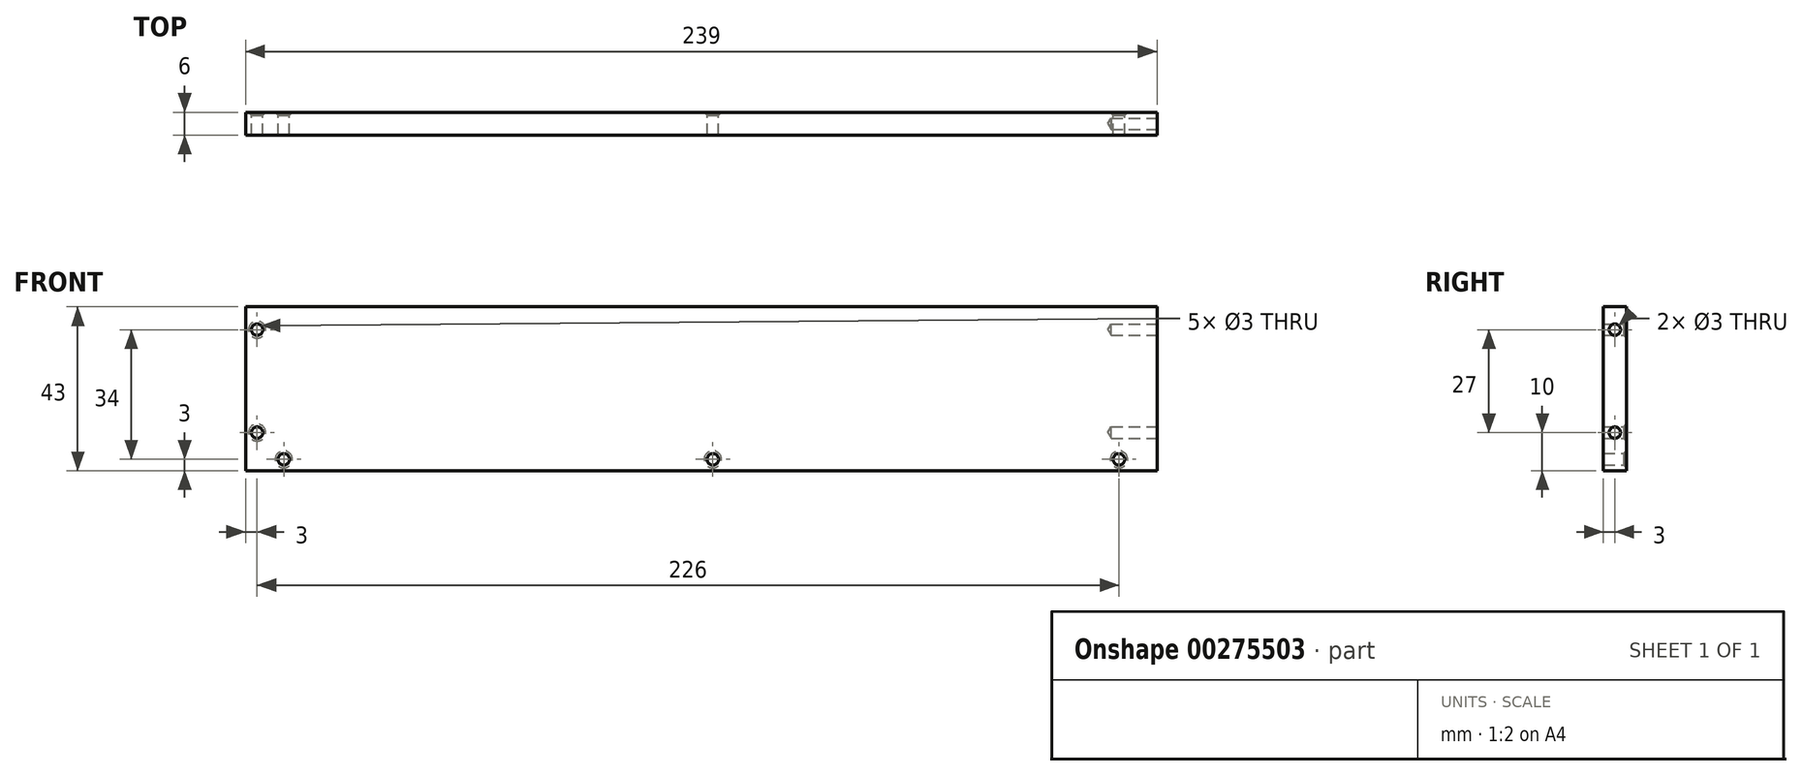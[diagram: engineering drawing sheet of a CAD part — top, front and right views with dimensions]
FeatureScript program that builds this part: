
annotation { "Feature Type Name" : "Feature", "Feature Type Description" : "" }
export const myFeature = defineFeature(function(context is Context, id is Id, definition is map)
    precondition{}
    {
        {
            var Q0;
            Q0=qCreatedBy(makeId("Top.planeOp"),FACE);
            var sketch = newSketch(context, id + "F0", { "sketchPlane" : qUnion([Q0])});
            skLineSegment(sketch, "E0.bottom", {"start": v(0, 0) * mm, "end": v(239, 0) * mm});
            skLineSegment(sketch, "E0.top", {"start": v(0, 6) * mm, "end": v(239, 6) * mm});
            skLineSegment(sketch, "E0.left", {"start": v(0, 0) * mm, "end": v(0, 6) * mm});
            skLineSegment(sketch, "E0.right", {"start": v(239, 0) * mm, "end": v(239, 6) * mm});
            skSolve(sketch);
        }
        {
            var Q0;
            Q0=makeQuery(id+"F0.imprint","IMPRINT",FACE,{"disambiguationData":[TD([[makeQuery(id+"F0.imprint","IMPRINT",EDGE,{"derivedFrom":sQuery(id+"F0.wireOp",EDGE,"E0.bottom")}),1.0]])]});
            extrude(context, id + "F1", {"entities" : qUnion([Q0]), "depth" : 43 * mm});
        }
        {
            var Q0;
            Q0=makeQuery(id+"F1.opExtrude","SWEPT_FACE",FACE,{"disambiguationData":[OSD([sQuery(id+"F0.wireOp",EDGE,"E0.top")])]});
            var sketch = newSketch(context, id + "F2", { "sketchPlane" : qUnion([Q0])});
            skPoint(sketch, "E1", {"position": v(-229, 3) * mm});
            skPoint(sketch, "E1.positionSnap0", {"position": v(-239, 21.5) * mm});
            skPoint(sketch, "E2", {"position": v(-10, 3) * mm});
            skPoint(sketch, "E2.positionSnap0", {"position": v(0, 21.5) * mm});
            skPoint(sketch, "E3", {"position": v(-122.5, 3) * mm});
            skSolve(sketch);
        }
        {
            var Q0;
            Q0=sQuery(id+"F2.wireOp",VERTEX,"E1");
            var Q1;
            Q1=sQuery(id+"F2.wireOp",VERTEX,"E3");
            var Q2;
            Q2=sQuery(id+"F2.wireOp",VERTEX,"E2");
            var Q3;
            Q3=makeQuery(id+"F1.opExtrude","SWEPT_BODY",BODY,{"disambiguationData":[OSD([sQuery(id+"F0.wireOp",EDGE,"E0.bottom"),sQuery(id+"F0.wireOp",EDGE,"E0.top"),sQuery(id+"F0.wireOp",EDGE,"E0.left"),sQuery(id+"F0.wireOp",EDGE,"E0.right")])]});
            hole(context, id + "F3", {"style" : HoleStyle.C_SINK, "endStyle" : HoleEndStyle.THROUGH, "holeDiameter" : 3 * mm, "cSinkDiameter" : 4.5 * mm, "cSinkAngle" : 90 * degree, "tappedDepth" : 12 * mm, "tapClearance" : 3, "locations" : qUnion([Q0, Q1, Q2]), "scope" : qUnion([Q3])});
        }
        {
            var Q0;
            Q0=makeQuery(id+"F1.opExtrude","SWEPT_FACE",FACE,{"disambiguationData":[OSD([sQuery(id+"F0.wireOp",EDGE,"E0.right")])]});
            var sketch = newSketch(context, id + "F4", { "sketchPlane" : qUnion([Q0])});
            skPoint(sketch, "E4", {"position": v(3, 37) * mm});
            skPoint(sketch, "E4.positionSnap0", {"position": v(3, 43) * mm});
            skPoint(sketch, "E5", {"position": v(3, 10) * mm});
            skPoint(sketch, "E5.positionSnap0", {"position": v(3, 0) * mm});
            skSolve(sketch);
        }
        {
            var Q0;
            Q0=sQuery(id+"F4.wireOp",VERTEX,"E4");
            var Q1;
            Q1=sQuery(id+"F4.wireOp",VERTEX,"E5");
            var Q2;
            Q2=makeQuery(id+"F1.opExtrude","SWEPT_BODY",BODY,{"disambiguationData":[OSD([sQuery(id+"F0.wireOp",EDGE,"E0.bottom"),sQuery(id+"F0.wireOp",EDGE,"E0.top"),sQuery(id+"F0.wireOp",EDGE,"E0.left"),sQuery(id+"F0.wireOp",EDGE,"E0.right")])]});
            hole(context, id + "F5", {"style" : HoleStyle.SIMPLE, "endStyle" : HoleEndStyle.BLIND, "holeDiameter" : 3 * mm, "holeDepth" : 12 * mm, "tappedDepth" : 12 * mm, "tapClearance" : 3, "locations" : qUnion([Q0, Q1]), "scope" : qUnion([Q2])});
        }
        {
            var Q0;
            Q0=makeQuery(id+"F1.opExtrude","SWEPT_FACE",FACE,{"disambiguationData":[OSD([sQuery(id+"F0.wireOp",EDGE,"E0.top")])]});
            var sketch = newSketch(context, id + "F6", { "sketchPlane" : qUnion([Q0])});
            skPoint(sketch, "E6", {"position": v(-3, 10) * mm});
            skPoint(sketch, "E7", {"position": v(-3, 37) * mm});
            skSolve(sketch);
        }
        {
            var Q0;
            Q0=sQuery(id+"F6.wireOp",VERTEX,"E7");
            var Q1;
            Q1=sQuery(id+"F6.wireOp",VERTEX,"E6");
            var Q2;
            Q2=makeQuery(id+"F1.opExtrude","SWEPT_BODY",BODY,{"disambiguationData":[OSD([sQuery(id+"F0.wireOp",EDGE,"E0.bottom"),sQuery(id+"F0.wireOp",EDGE,"E0.top"),sQuery(id+"F0.wireOp",EDGE,"E0.left"),sQuery(id+"F0.wireOp",EDGE,"E0.right")])]});
            hole(context, id + "F7", {"style" : HoleStyle.C_SINK, "endStyle" : HoleEndStyle.THROUGH, "holeDiameter" : 3 * mm, "cSinkDiameter" : 4.5 * mm, "cSinkAngle" : 90 * degree, "tappedDepth" : 12 * mm, "tapClearance" : 3, "locations" : qUnion([Q0, Q1]), "scope" : qUnion([Q2])});
        }
    });
